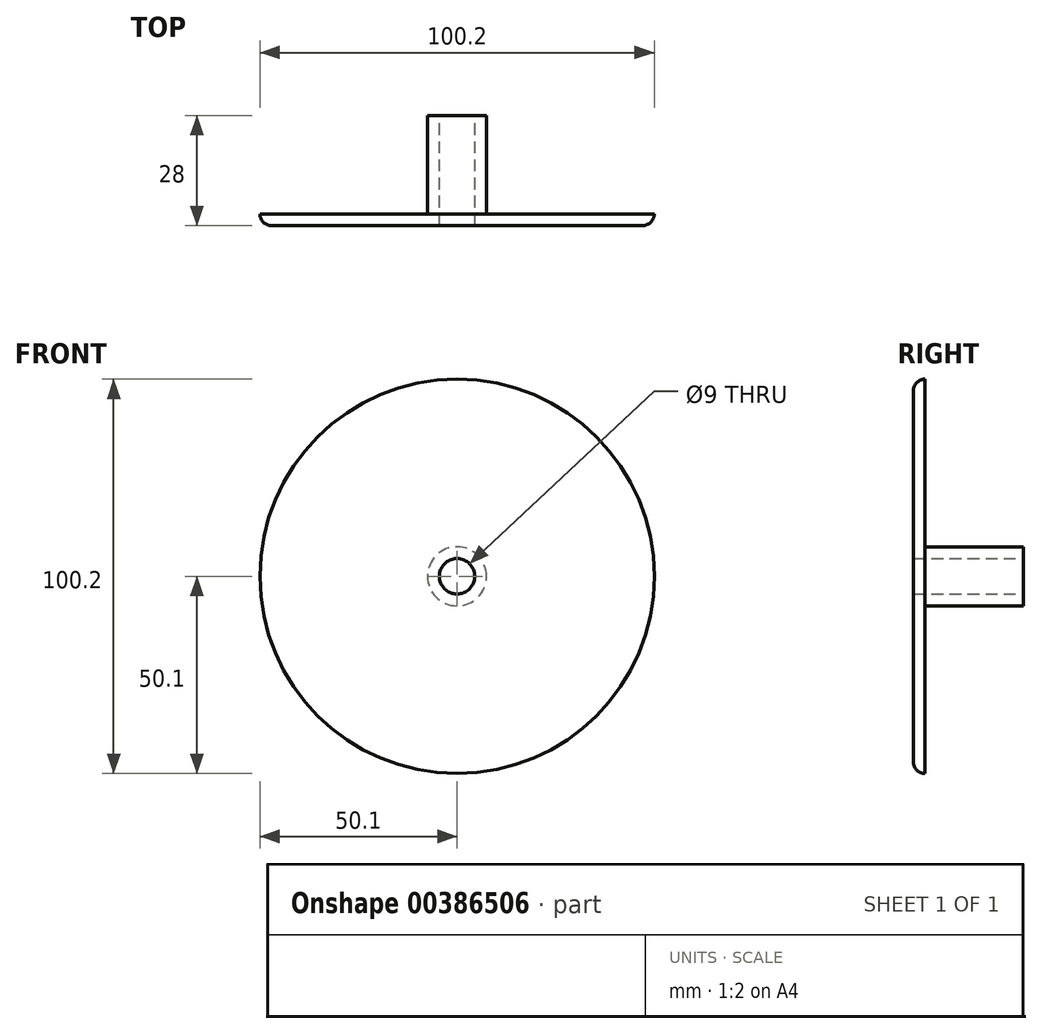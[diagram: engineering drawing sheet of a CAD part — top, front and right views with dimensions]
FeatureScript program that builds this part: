
annotation { "Feature Type Name" : "Feature", "Feature Type Description" : "" }
export const myFeature = defineFeature(function(context is Context, id is Id, definition is map)
    precondition{}
    {
        {
            var Q0;
            Q0=qCreatedBy(makeId("Front.planeOp"),FACE);
            var sketch = newSketch(context, id + "F0", { "sketchPlane" : qUnion([Q0])});
            skCircle(sketch, "E0", {"center": v(0, 0) * mm, "radius": 50.1 * mm});
            skCircle(sketch, "E1", {"center": v(0, 0) * mm, "radius": 4.5 * mm});
            skSolve(sketch);
        }
        {
            var Q0;
            Q0=makeQuery(id+"F0.imprint","IMPRINT",FACE,{"disambiguationData":[TD([[makeQuery(id+"F0.imprint","IMPRINT",EDGE,{"derivedFrom":sQuery(id+"F0.wireOp",EDGE,"E0")}),1.0]])]});
            extrude(context, id + "F1", {"entities" : qUnion([Q0]), "depth" : 3 * mm});
        }
        {
            var Q0;
            Q0=makeQuery(id+"F1.opExtrude","CAP_FACE",FACE,{"disambiguationData":[OSD([sQuery(id+"F0.wireOp",EDGE,"E0"),sQuery(id+"F0.wireOp",EDGE,"E1")])],"isStart":true});
            var sketch = newSketch(context, id + "F2", { "sketchPlane" : qUnion([Q0])});
            skCircle(sketch, "E2", {"center": v(0, 0) * mm, "radius": 7.5 * mm});
            skCircle(sketch, "E3", {"center": v(0, 0) * mm, "radius": 4.5 * mm});
            skSolve(sketch);
        }
        {
            var Q0;
            Q0 = qSketchRegion(id + "F2", true);
            extrude(context, id + "F3", {"entities" : qUnion([Q0]), "operationType" : NewBodyOperationType.ADD, "depth" : 25 * mm});
        }
        {
            var Q0;
            Q0=makeQuery(id+"F1.opExtrude","CAP_EDGE",EDGE,{"disambiguationData":[OSD([sQuery(id+"F0.wireOp",EDGE,"E0")])],"isStart":false});
            fillet(context, id + "F4", {"entities" : qUnion([Q0]), "radius" : 3 * mm, "tangentPropagation" : true, "allowEdgeOverflow" : false});
        }
    });
